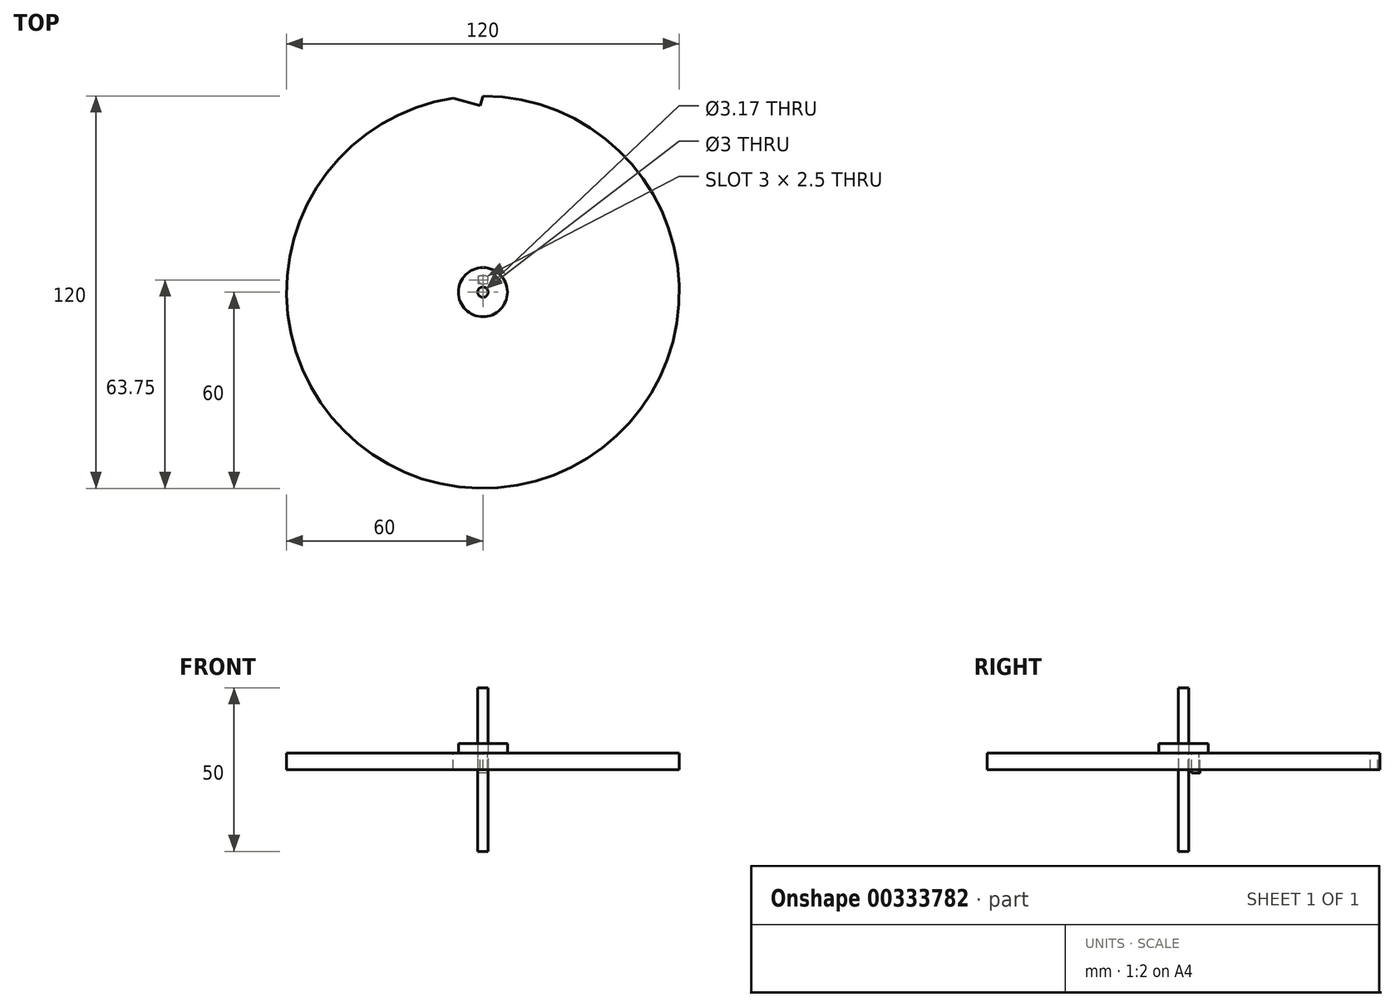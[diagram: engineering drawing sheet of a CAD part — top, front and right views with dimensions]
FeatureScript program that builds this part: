
annotation { "Feature Type Name" : "Feature", "Feature Type Description" : "" }
export const myFeature = defineFeature(function(context is Context, id is Id, definition is map)
    precondition{}
    {
        {
            assignVariable(context, id + "F0", {"name" : "faceWidth", "anyValue" : 5});
        }
        {
            var Q0;
            Q0=qCreatedBy(makeId("Top.planeOp"),FACE);
            var sketch = newSketch(context, id + "F1", { "sketchPlane" : qUnion([Q0])});
            skCircle(sketch, "E0", {"center": v(0, 0) * mm, "radius": 60 * mm});
            skSolve(sketch);
        }
        {
            var Q0;
            Q0 = qSketchRegion(id + "F1", true);
            extrude(context, id + "F2", {"entities" : qUnion([Q0]), "depth" : (getVariable(context, 'faceWidth')) * mm});
        }
        {
            var Q0;
            Q0=makeQuery(id+"F2.opExtrude","CAP_FACE",FACE,{"disambiguationData":[OSD([sQuery(id+"F1.wireOp",EDGE,"E0")])],"isStart":false});
            var sketch = newSketch(context, id + "F3", { "sketchPlane" : qUnion([Q0])});
            skLineSegment(sketch, "E1", {"start": v(0, 60) * mm, "end": v(-0.78, 57.1) * mm});
            skLineSegment(sketch, "E2", {"start": v(-0.78, 57.1) * mm, "end": v(-9.04, 59.32) * mm});
            skSolve(sketch);
        }
        {
            var Q0;
            Q0 = qSketchRegion(id + "F3", true);
            var Q1;
            {var subQ0=sQuery(id+"F3.wireOp",EDGE,"E1");Q1=makeQuery(id+"F3.imprint","IMPRINT",FACE,{"disambiguationData":[TD([[makeQuery(id+"F3.imprint","IMPRINT",EDGE,{"derivedFrom":subQ0}),-1.0]])]});}
            extrude(context, id + "F4", {"entities" : qUnion([Q0, Q1]), "operationType" : NewBodyOperationType.REMOVE, "endBound" : BoundingType.THROUGH_ALL, "oppositeDirection" : true, "depth" : 25 * mm});
        }
        {
            assignVariable(context, id + "F5", {"name" : "keyStopperWidth", "anyValue" : 3});
        }
        {
            assignVariable(context, id + "F6", {"name" : "shaftLength", "anyValue" : 50});
        }
        {
            var Q0;
            Q0=makeQuery(id+"F2.opExtrude","CAP_FACE",FACE,{"disambiguationData":[OSD([sQuery(id+"F1.wireOp",EDGE,"E0")])],"isStart":false});
            var sketch = newSketch(context, id + "F7", { "sketchPlane" : qUnion([Q0])});
            skCircle(sketch, "E3", {"center": v(0, 0) * mm, "radius": 0.5 * mm});
            skCircle(sketch, "E4", {"center": v(0, 0) * mm, "radius": 5 * mm});
            skLineSegment(sketch, "E5", {"start": v(0, 5) * mm, "end": v(0, 4) * mm});
            skArc(sketch, "E6.0.startCap", {"start": v(-1.5, 5) * mm, "mid": v(0, 6.5) * mm, "end": v(1.5, 5) * mm});
            skArc(sketch, "E6.0.endCap", {"start": v(1.5, 4) * mm, "mid": v(0, 2.5) * mm, "end": v(-1.5, 4) * mm});
            skLineSegment(sketch, "E6.0.left", {"start": v(1.5, 5) * mm, "end": v(1.5, 4) * mm});
            skLineSegment(sketch, "E6.0.right", {"start": v(-1.5, 5) * mm, "end": v(-1.5, 4) * mm});
            skLineSegment(sketch, "E7", {"start": v(5, 0) * mm, "end": v(4, 0) * mm});
            skLineSegment(sketch, "E8", {"start": v(0, -5) * mm, "end": v(0, -4) * mm});
            skLineSegment(sketch, "E9", {"start": v(-5, 0) * mm, "end": v(-4, 0) * mm});
            skArc(sketch, "E10.0.startCap", {"start": v(-5, -1.5) * mm, "mid": v(-6.5, 0) * mm, "end": v(-5, 1.5) * mm});
            skArc(sketch, "E10.0.endCap", {"start": v(-4, 1.5) * mm, "mid": v(-2.5, 0) * mm, "end": v(-4, -1.5) * mm});
            skLineSegment(sketch, "E10.0.left", {"start": v(-5, 1.5) * mm, "end": v(-4, 1.5) * mm});
            skLineSegment(sketch, "E10.0.right", {"start": v(-5, -1.5) * mm, "end": v(-4, -1.5) * mm});
            skArc(sketch, "E10.1.startCap", {"start": v(5, 1.5) * mm, "mid": v(6.5, 0) * mm, "end": v(5, -1.5) * mm});
            skArc(sketch, "E10.1.endCap", {"start": v(4, -1.5) * mm, "mid": v(2.5, 0) * mm, "end": v(4, 1.5) * mm});
            skLineSegment(sketch, "E10.1.left", {"start": v(5, -1.5) * mm, "end": v(4, -1.5) * mm});
            skLineSegment(sketch, "E10.1.right", {"start": v(5, 1.5) * mm, "end": v(4, 1.5) * mm});
            skArc(sketch, "E10.2.startCap", {"start": v(1.5, -5) * mm, "mid": v(0, -6.5) * mm, "end": v(-1.5, -5) * mm});
            skArc(sketch, "E10.2.endCap", {"start": v(-1.5, -4) * mm, "mid": v(0, -2.5) * mm, "end": v(1.5, -4) * mm});
            skLineSegment(sketch, "E10.2.left", {"start": v(-1.5, -5) * mm, "end": v(-1.5, -4) * mm});
            skLineSegment(sketch, "E10.2.right", {"start": v(1.5, -5) * mm, "end": v(1.5, -4) * mm});
            skCircle(sketch, "E11", {"center": v(0, 0) * mm, "radius": 1.5 * mm});
            skSolve(sketch);
        }
        {
            var Q0;
            {var subQ2=sQuery(id+"F7.wireOp",EDGE,"E6.0.endCap");Q0=makeQuery(id+"F7.imprint","IMPRINT",FACE,{"disambiguationData":[TD([[makeQuery(id+"F7.imprint","IMPRINT",EDGE,{"derivedFrom":subQ2}),1.0]])]});}
            var Q1;
            Q1=makeQuery(id+"F7.imprint","IMPRINT",FACE,{"disambiguationData":[TD([[makeQuery(id+"F7.imprint","IMPRINT",EDGE,{"derivedFrom":sQuery(id+"F7.wireOp",EDGE,"E11")}),1.0]])]});
            var Q2;
            Q2=makeQuery(id+"F7.imprint","IMPRINT",FACE,{"disambiguationData":[TD([[makeQuery(id+"F7.imprint","IMPRINT",EDGE,{"derivedFrom":sQuery(id+"F7.wireOp",EDGE,"E3")}),1.0]])]});
            extrude(context, id + "F8", {"entities" : qUnion([Q0, Q1, Q2]), "operationType" : NewBodyOperationType.REMOVE, "endBound" : BoundingType.THROUGH_ALL, "oppositeDirection" : true, "depth" : 25 * mm});
        }
        {
            var Q0;
            {var subQ2=sQuery(id+"F7.wireOp",EDGE,"E6.0.endCap");Q0=makeQuery(id+"F7.imprint","IMPRINT",FACE,{"disambiguationData":[TD([[makeQuery(id+"F7.imprint","IMPRINT",EDGE,{"derivedFrom":subQ2}),1.0]])]});}
            extrude(context, id + "F9", {"entities" : qUnion([Q0]), "oppositeDirection" : true, "depth" : (getVariable(context, 'faceWidth') + 1) * mm});
        }
        {
            var Q0;
            Q0=makeQuery(id+"F2.opExtrude","CAP_FACE",FACE,{"disambiguationData":[OSD([sQuery(id+"F1.wireOp",EDGE,"E0")])],"isStart":false});
            var sketch = newSketch(context, id + "F10", { "sketchPlane" : qUnion([Q0])});
            skCircle(sketch, "E12", {"center": v(0, 0) * mm, "radius": 7.5 * mm});
            skCircle(sketch, "E13", {"center": v(0, 0) * mm, "radius": 1.59 * mm});
            skSolve(sketch);
        }
        {
            var Q0;
            Q0 = qSketchRegion(id + "F10", true);
            extrude(context, id + "F11", {"entities" : qUnion([Q0]), "depth" : (getVariable(context, 'keyStopperWidth')) * mm});
        }
        {
            var Q0;
            Q0=qCreatedBy(makeId("Top.planeOp"),FACE);
            var sketch = newSketch(context, id + "F12", { "sketchPlane" : qUnion([Q0])});
            skCircle(sketch, "E14", {"center": v(0, 0) * mm, "radius": 1.59 * mm});
            skSolve(sketch);
        }
        {
            var Q0;
            Q0 = qSketchRegion(id + "F12", true);
            extrude(context, id + "F13", {"entities" : qUnion([Q0]), "endBound" : BoundingType.SYMMETRIC, "depth" : (getVariable(context, 'shaftLength')) * mm});
        }
    });
